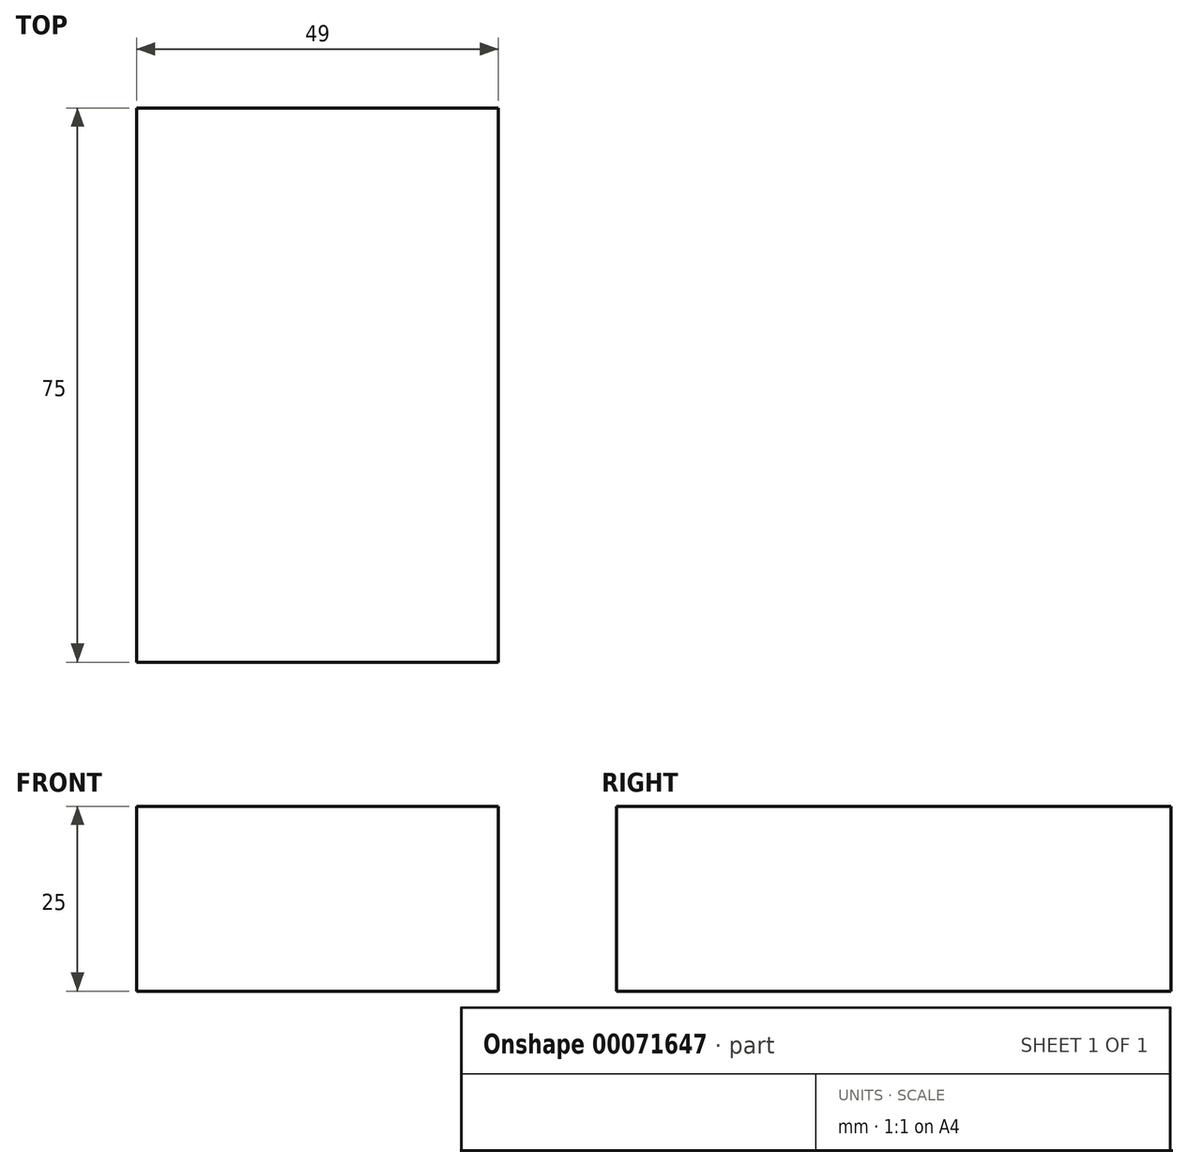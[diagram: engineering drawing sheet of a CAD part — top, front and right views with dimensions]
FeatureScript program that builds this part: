
annotation { "Feature Type Name" : "Feature", "Feature Type Description" : "" }
export const myFeature = defineFeature(function(context is Context, id is Id, definition is map)
    precondition{}
    {
        {
            var Q0;
            Q0=qCreatedBy(makeId("Top.planeOp"),FACE);
            var sketch = newSketch(context, id + "F0", { "sketchPlane" : qUnion([Q0])});
            skLineSegment(sketch, "E0.rect.bottom", {"start": v(24.5, 37.5) * mm, "end": v(-24.5, 37.5) * mm});
            skLineSegment(sketch, "E0.rect.top", {"start": v(24.5, -37.5) * mm, "end": v(-24.5, -37.5) * mm});
            skLineSegment(sketch, "E0.rect.left", {"start": v(24.5, 37.5) * mm, "end": v(24.5, -37.5) * mm});
            skLineSegment(sketch, "E0.rect.right", {"start": v(-24.5, 37.5) * mm, "end": v(-24.5, -37.5) * mm});
            skPoint(sketch, "E0.rect.middle", {"position": v(0, 0) * mm});
            skSolve(sketch);
        }
        {
            var Q0;
            Q0 = qSketchRegion(id + "F0", true);
            extrude(context, id + "F1", {"entities" : qUnion([Q0]), "depth" : 25 * mm});
        }
    });
